# Revit family: 2CKA006800A2514
name_source: partatom
category: Elektroinstallationen
revit_build: Autodesk Revit 2017 (Build: 20160225_1515(x64)
units: mm (PartAtom-declared; Revit-internal decimal feet)

## family parameters
Basisbauteil = Fläche
Beim Laden mit Abzugskörper schneiden = Nein
Bemaßung runder Anschluss = Durchmesser verwenden
Beschriftungsausrichtung beibehalten = Nein
Gemeinsam genutzt = Nein
Raumberechnungspunkt = Nein
Teiletyp = Normal

## types (1)
- 2CKA006800A2514
    Art des Zubehörs = Funkmodul
    BIM = https://media.live.bim.site
    BIMSITE_PRODUCT_ID = fe110aea17587d31f36e217aa704544c4bba5982
    Beschreibung = Busch-Rauchalarm RF, Sicherheitstechnik, Busch-Rauchalarm ProfessionalLINE, Busch-Rauchalarm RF Funkmodul für den Einsatz im Busch-Rauchalarm/-Wärmealarm (6833/01-84 und 6835/01-84). Zur drahtlosen Vernetzung von bis zu 20 Funk-Teilnehmern. Nach VdS Richtlinie 3515 geprüft. Geeignet für die Anbindung des Busch-Rauchalarm/-Wärmealarm an externe Systeme wie Busch-free@home in Kombination mit dem Busch-free@homeAlarm-Stick. Mit fest eingebauter Lithiumbatterie. Batterielebensdauer mind. 10 Jahre. Funkfrequenz: 868 MHz Reichweite: max. 100 m im Freien, max. 30 m im Gebäude.
    Datenblatt = https://media.live.bim.site
    GTIN = 4011395137451
    Gerätebreite [mm] = 59
    Gerätehöhe [mm] = 36
    Gerätetiefe [mm] = 27
    Gewicht [kg/m] = 0.26
    HAN = 2CKA006800A2514
    HeinzeBIM = https://www.heinze.de
    Hersteller = Busch-Jaeger
    Ist System = Nein
    Ist Zubehör = Nein
    Produktseite = https://media.live.bim.site
    TYPE = 6828
    Typname = Busch-Rauchalarm RF, Sicherheitstechnik, Busch-Rauchalarm ProfessionalLINE
    URL = https://www.busch-jaeger.de
    Vorgabe-Ansicht = 1219 mm

## geometry (parser evidence)
native form markers: Sweep x3
no freeform markers — native parametric forms only
